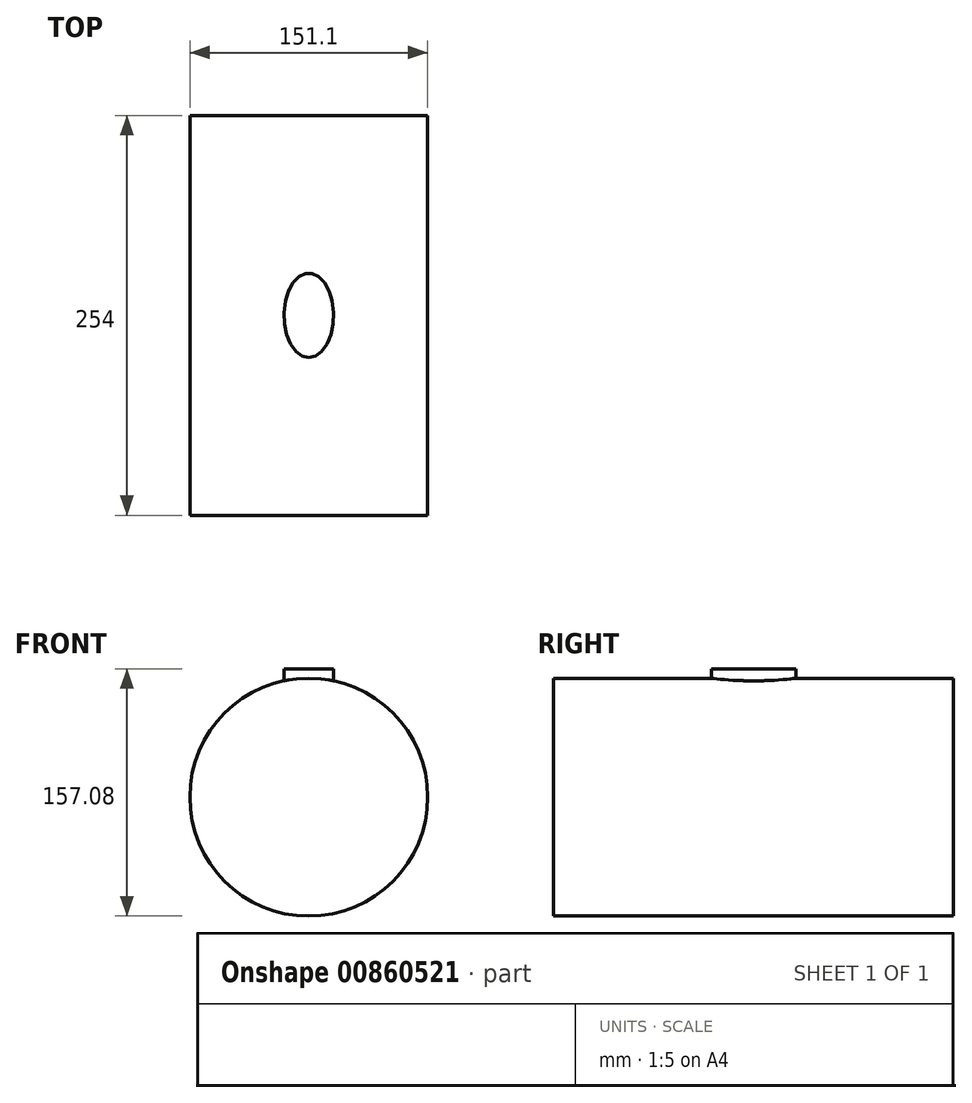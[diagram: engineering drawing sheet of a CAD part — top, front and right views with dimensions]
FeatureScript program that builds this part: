
annotation { "Feature Type Name" : "Feature", "Feature Type Description" : "" }
export const myFeature = defineFeature(function(context is Context, id is Id, definition is map)
    precondition{}
    {
        {
            var Q0;
            Q0=qCreatedBy(makeId("Front.planeOp"),FACE);
            var sketch = newSketch(context, id + "F0", { "sketchPlane" : qUnion([Q0])});
            skCircle(sketch, "E0", {"center": v(0, 0) * mm, "radius": 75.55 * mm});
            skSolve(sketch);
        }
        {
            var Q0;
            Q0 = qSketchRegion(id + "F0", true);
            extrude(context, id + "F1", {"entities" : qUnion([Q0]), "depth" : 254 * mm, "offsetDistance" : 25.4 * mm, "symmetric" : true});
        }
        {
            var Q0;
            Q0=qCreatedBy(makeId("Top.planeOp"),FACE);
            cPlane(context, id + "F2", {"entities" : qUnion([Q0]), "cplaneType" : CPlaneType.OFFSET, "offset" : 75.18 * mm, "width" : 152.4 * mm, "height" : 152.4 * mm});
        }
        {
            var Q0;
            Q0=qCreatedBy(id+"F2.planeOp",FACE);
            var sketch = newSketch(context, id + "F3", { "sketchPlane" : qUnion([Q0])});
            skEllipse(sketch, "E1", {"center": v(0, 0) * mm, "majorRadius": 26.8 * mm, "minorRadius": 15.77 * mm, "majorAxis": v(0, -1)});
            skLineSegment(sketch, "E2.bottom", {"start": v(-24.32, 93.72) * mm, "end": v(28.03, 93.72) * mm});
            skLineSegment(sketch, "E2.top", {"start": v(-24.32, 90.23) * mm, "end": v(28.03, 90.23) * mm});
            skLineSegment(sketch, "E2.left", {"start": v(-24.32, 93.72) * mm, "end": v(-24.32, 90.23) * mm});
            skLineSegment(sketch, "E2.right", {"start": v(28.03, 93.72) * mm, "end": v(28.03, 90.23) * mm});
            skLineSegment(sketch, "E3.0.1.0", {"start": v(-24.32, 83.3) * mm, "end": v(28.03, 83.3) * mm});
            skLineSegment(sketch, "E3.0.1.1", {"start": v(-24.32, 79.81) * mm, "end": v(28.03, 79.81) * mm});
            skLineSegment(sketch, "E3.0.1.2", {"start": v(28.03, 83.3) * mm, "end": v(28.03, 79.81) * mm});
            skLineSegment(sketch, "E3.0.1.3", {"start": v(-24.32, 83.3) * mm, "end": v(-24.32, 79.81) * mm});
            skLineSegment(sketch, "E3.0.2.0", {"start": v(-24.32, 72.89) * mm, "end": v(28.03, 72.89) * mm});
            skLineSegment(sketch, "E3.0.2.1", {"start": v(-24.32, 69.4) * mm, "end": v(28.03, 69.4) * mm});
            skLineSegment(sketch, "E3.0.2.2", {"start": v(28.03, 72.89) * mm, "end": v(28.03, 69.4) * mm});
            skLineSegment(sketch, "E3.0.2.3", {"start": v(-24.32, 72.89) * mm, "end": v(-24.32, 69.4) * mm});
            skLineSegment(sketch, "E3.0.3.0", {"start": v(-24.32, 62.48) * mm, "end": v(28.03, 62.48) * mm});
            skLineSegment(sketch, "E3.0.3.1", {"start": v(-24.32, 58.99) * mm, "end": v(28.03, 58.99) * mm});
            skLineSegment(sketch, "E3.0.3.2", {"start": v(28.03, 62.48) * mm, "end": v(28.03, 58.99) * mm});
            skLineSegment(sketch, "E3.0.3.3", {"start": v(-24.32, 62.48) * mm, "end": v(-24.32, 58.99) * mm});
            skLineSegment(sketch, "E3.direction1", {"start": v(-24.32, 90.23) * mm, "end": v(1.08, 90.23) * mm, "construction": true});
            skLineSegment(sketch, "E3.direction2", {"start": v(-24.32, 90.23) * mm, "end": v(-24.32, 79.81) * mm, "construction": true});
            skSolve(sketch);
        }
        {
            var Q0;
            Q0=makeQuery(id+"F3.imprint","IMPRINT",FACE,{"disambiguationData":[TD([[makeQuery(id+"F3.imprint","IMPRINT",EDGE,{"derivedFrom":sQuery(id+"F3.wireOp",EDGE,"E1")}),1.0]])]});
            extrude(context, id + "F4", {"entities" : qUnion([Q0]), "operationType" : NewBodyOperationType.ADD, "depth" : 12.7 * mm, "offsetDistance" : 25.4 * mm, "symmetric" : true});
        }
    });
